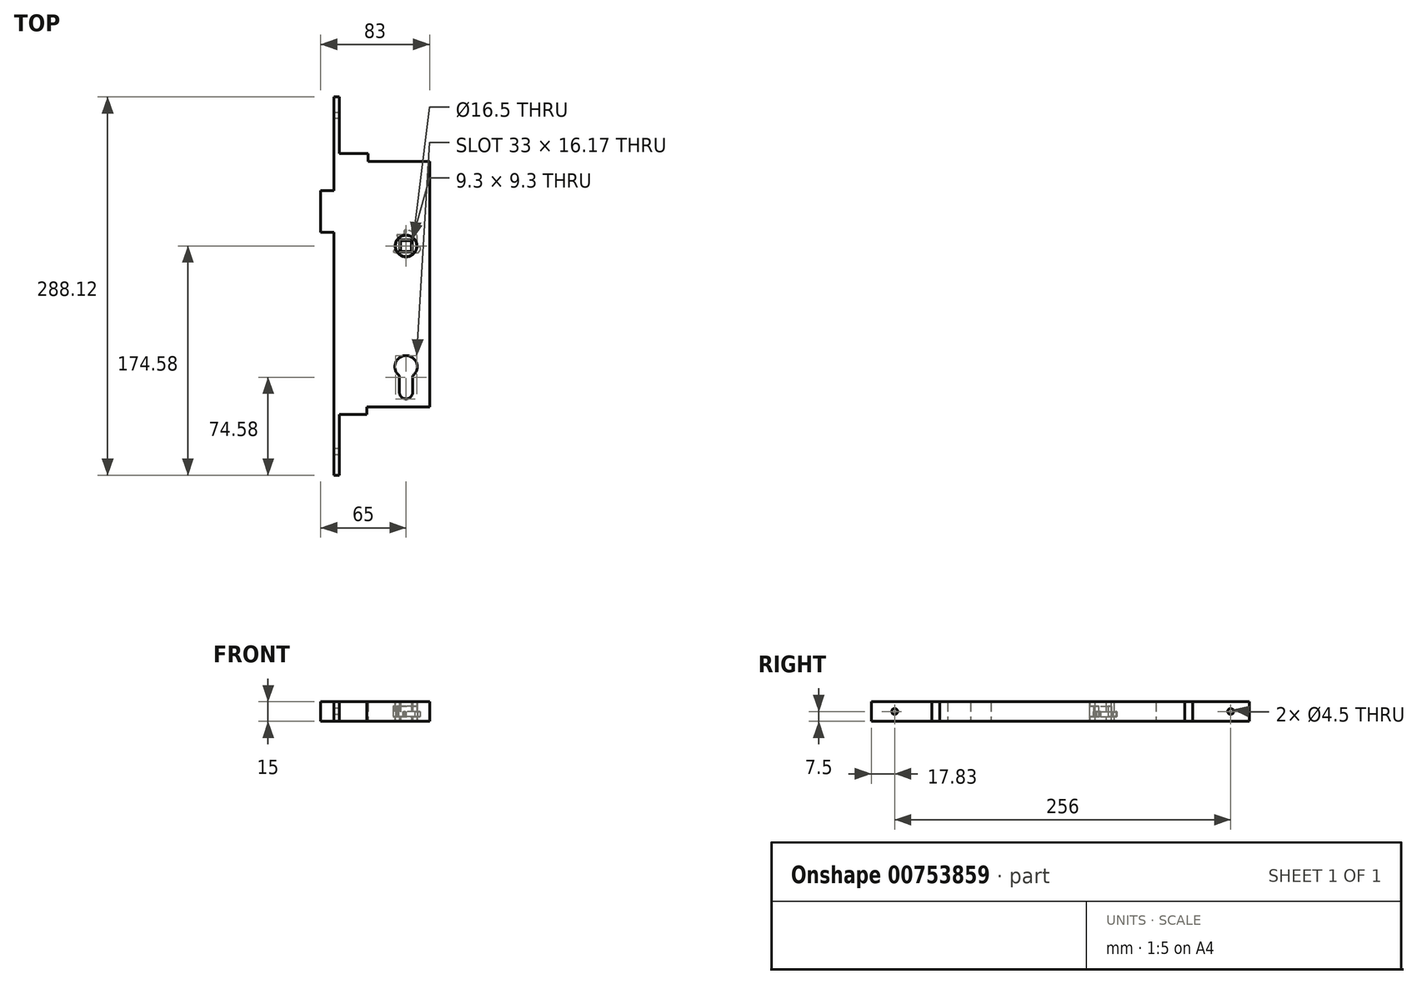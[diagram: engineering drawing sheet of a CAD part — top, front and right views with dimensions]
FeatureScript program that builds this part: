
annotation { "Feature Type Name" : "Feature", "Feature Type Description" : "" }
export const myFeature = defineFeature(function(context is Context, id is Id, definition is map)
    precondition{}
    {
        {
            var Q0;
            Q0=qCreatedBy(makeId("Top.planeOp"),FACE);
            var sketch = newSketch(context, id + "F0", { "sketchPlane" : qUnion([Q0])});
            skLineSegment(sketch, "E0.bottom", {"start": v(4.15, 4.15) * mm, "end": v(-4.15, 4.15) * mm});
            skLineSegment(sketch, "E0.top", {"start": v(4.15, -4.15) * mm, "end": v(-4.15, -4.15) * mm});
            skLineSegment(sketch, "E0.left", {"start": v(4.15, 4.15) * mm, "end": v(4.15, -4.15) * mm});
            skLineSegment(sketch, "E0.right", {"start": v(-4.15, 4.15) * mm, "end": v(-4.15, -4.15) * mm});
            skPoint(sketch, "E0.middle", {"position": v(0, 0) * mm});
            skCircle(sketch, "E1", {"center": v(0, 0) * mm, "radius": 8.15 * mm});
            skSolve(sketch);
        }
        {
            var Q0;
            Q0=makeQuery(id+"F0.imprint","IMPRINT",FACE,{"disambiguationData":[TD([[makeQuery(id+"F0.imprint","IMPRINT",EDGE,{"derivedFrom":sQuery(id+"F0.wireOp",EDGE,"E0.bottom")}),-1.0]])]});
            extrude(context, id + "F1", {"entities" : qUnion([Q0]), "depth" : 3.5 * mm, "offsetDistance" : 25 * mm});
        }
        {
            var Q0;
            Q0=makeQuery(id+"F1.opExtrude","CAP_FACE",FACE,{"disambiguationData":[OSD([sQuery(id+"F0.wireOp",EDGE,"E0.bottom"),sQuery(id+"F0.wireOp",EDGE,"E0.top"),sQuery(id+"F0.wireOp",EDGE,"E0.left"),sQuery(id+"F0.wireOp",EDGE,"E0.right"),sQuery(id+"F0.wireOp",EDGE,"E1")])],"isStart":false});
            var sketch = newSketch(context, id + "F2", { "sketchPlane" : qUnion([Q0])});
            skCircle(sketch, "E2", {"center": v(0, 0) * mm, "radius": 8.53 * mm});
            skLineSegment(sketch, "E3", {"start": v(-4.15, 4.15) * mm, "end": v(7.23, -7.2) * mm, "construction": true});
            skLineSegment(sketch, "E4", {"start": v(7.23, -7.2) * mm, "end": v(-8.21, 8.2) * mm, "construction": true});
            skLineSegment(sketch, "E5", {"start": v(0, 0) * mm, "end": v(7.32, 7.33) * mm, "construction": true});
            skLineSegment(sketch, "E6", {"start": v(7.32, 7.33) * mm, "end": v(-7.76, -7.78) * mm, "construction": true});
            skLineSegment(sketch, "E7", {"start": v(0, 8.53) * mm, "end": v(-7.56, 8.53) * mm});
            skLineSegment(sketch, "E8", {"start": v(8.53, 0) * mm, "end": v(8.53, 8) * mm});
            skLineSegment(sketch, "E9", {"start": v(-7.56, 8.53) * mm, "end": v(-5.76, 5.76) * mm});
            skPoint(sketch, "E10", {"position": v(-2.56, 8.53) * mm});
            skLineSegment(sketch, "E11", {"start": v(8.53, 0) * mm, "end": v(10.8, -1.06) * mm});
            skLineSegment(sketch, "E12", {"start": v(10.8, -1.06) * mm, "end": v(10.8, -3.06) * mm});
            skLineSegment(sketch, "E13", {"start": v(9.01, -5.5) * mm, "end": v(6.51, -5.5) * mm});
            skPoint(sketch, "E14", {"position": v(9.01, -5.5) * mm});
            skPoint(sketch, "E15", {"position": v(10.8, -3.06) * mm});
            skLineSegment(sketch, "E16", {"start": v(10.8, -3.06) * mm, "end": v(9.01, -5.5) * mm});
            skPoint(sketch, "E17", {"position": v(0, 12.53) * mm});
            skLineSegment(sketch, "E18", {"start": v(8.53, 0) * mm, "end": v(8.53, -5.5) * mm, "construction": true});
            skArc(sketch, "E19", {"start": v(8.53, 8) * mm, "mid": v(4.54, 10.78) * mm, "end": v(0, 12.53) * mm});
            skPoint(sketch, "E20", {"position": v(-1.56, 9.53) * mm});
            skLineSegment(sketch, "E21", {"start": v(-2.56, 8.53) * mm, "end": v(-1.56, 9.53) * mm});
            skPoint(sketch, "E22", {"position": v(-0.56, 9.53) * mm});
            skPoint(sketch, "E23", {"position": v(0, 11.53) * mm});
            skArc(sketch, "E24", {"start": v(-0.56, 9.53) * mm, "mid": v(-0.09, 10.47) * mm, "end": v(0, 11.53) * mm});
            skLineSegment(sketch, "E25", {"start": v(0, 12.53) * mm, "end": v(0, 11.53) * mm});
            skLineSegment(sketch, "E26", {"start": v(-0.56, 9.53) * mm, "end": v(-1.56, 9.53) * mm});
            skLineSegment(sketch, "E27", {"start": v(0, -4.4) * mm, "end": v(-13.74, -4.4) * mm, "construction": true});
            skPoint(sketch, "E28", {"position": v(-9.86, -4.4) * mm});
            skPoint(sketch, "E29", {"position": v(-6.86, -4.4) * mm});
            skLineSegment(sketch, "E30", {"start": v(-8.03, -1.4) * mm, "end": v(-8.03, -4.4) * mm, "construction": true});
            skLineSegment(sketch, "E31", {"start": v(-8.03, -1.4) * mm, "end": v(-9.86, -4.4) * mm});
            skLineSegment(sketch, "E32", {"start": v(-9.86, -4.4) * mm, "end": v(-8, -5.13) * mm});
            skLineSegment(sketch, "E33", {"start": v(-8, -5.13) * mm, "end": v(-6.74, -5.23) * mm});
            skSolve(sketch);
        }
        {
            var Q0;
            {var subQ0=sQuery(id+"F2.wireOp",EDGE,"E2");var subQ5=makeQuery(id+"F2.imprint","INTERSECT",VERTEX,{"derivedFrom":[subQ0,sQuery(id+"F2.wireOp",EDGE,"E7")]});Q0=makeQuery(id+"F2.imprint","IMPRINT",FACE,{"disambiguationData":[TD([[makeQuery(id+"F2.imprint","IMPRINT",EDGE,{"disambiguationData":[TD([[subQ5,-1.0]])],"derivedFrom":subQ0}),1.0]])]});}
            var Q1;
            {var subQ0=sQuery(id+"F2.wireOp",EDGE,"E7");var subQ1=sQuery(id+"F2.wireOp",EDGE,"E2");var subQ2=makeQuery(id+"F2.imprint","INTERSECT",VERTEX,{"derivedFrom":[subQ1,subQ0]});Q1=makeQuery(id+"F2.imprint","IMPRINT",FACE,{"disambiguationData":[TD([[makeQuery(id+"F2.imprint","IMPRINT",EDGE,{"disambiguationData":[TD([[subQ2,-1.0]])],"derivedFrom":subQ1}),-1.0]])]});}
            var Q2;
            {var subQ0=sQuery(id+"F2.wireOp",EDGE,"E8");Q2=makeQuery(id+"F2.imprint","IMPRINT",FACE,{"disambiguationData":[TD([[makeQuery(id+"F2.imprint","IMPRINT",EDGE,{"derivedFrom":subQ0}),1.0]])]});}
            var Q3;
            {var subQ1=sQuery(id+"F2.wireOp",EDGE,"E11");Q3=makeQuery(id+"F2.imprint","IMPRINT",FACE,{"disambiguationData":[TD([[makeQuery(id+"F2.imprint","IMPRINT",EDGE,{"derivedFrom":subQ1}),-1.0]])]});}
            var Q4;
            {var subQ4=sQuery(id+"F2.wireOp",EDGE,"E32");Q4=makeQuery(id+"F2.imprint","IMPRINT",FACE,{"disambiguationData":[TD([[makeQuery(id+"F2.imprint","IMPRINT",EDGE,{"derivedFrom":subQ4}),1.0]])]});}
            var Q5;
            Q5=makeQuery(id+"F2.imprint","IMPRINT",FACE,{"disambiguationData":[TD([[makeQuery(id+"F2.imprint","IMPRINT",EDGE,{"derivedFrom":makeQuery(id+"F1.opExtrude","CAP_EDGE",EDGE,{"disambiguationData":[OSD([sQuery(id+"F0.wireOp",EDGE,"E0.bottom")])],"isStart":false})}),-1.0]])]});
            extrude(context, id + "F3", {"entities" : qUnion([Q0, Q1, Q2, Q3, Q4, Q5]), "operationType" : NewBodyOperationType.ADD, "depth" : 3.8 * mm, "offsetDistance" : 25 * mm});
        }
        {
            var Q0;
            Q0=makeQuery(id+"F2.imprint","IMPRINT",FACE,{"disambiguationData":[TD([[makeQuery(id+"F2.imprint","IMPRINT",EDGE,{"derivedFrom":makeQuery(id+"F1.opExtrude","CAP_EDGE",EDGE,{"disambiguationData":[OSD([sQuery(id+"F0.wireOp",EDGE,"E0.bottom")])],"isStart":false})}),-1.0]])]});
            extrude(context, id + "F4", {"entities" : qUnion([Q0]), "operationType" : NewBodyOperationType.ADD, "depth" : 11.5 * mm, "offsetDistance" : 25 * mm});
        }
        {
            var Q0;
            {var subQ0=sQuery(id+"F2.wireOp",EDGE,"E2");var subQ5=makeQuery(id+"F2.imprint","INTERSECT",VERTEX,{"derivedFrom":[subQ0,sQuery(id+"F2.wireOp",EDGE,"E7")]});Q0=makeQuery(id+"F2.imprint","IMPRINT",FACE,{"disambiguationData":[TD([[makeQuery(id+"F2.imprint","IMPRINT",EDGE,{"disambiguationData":[TD([[subQ5,-1.0]])],"derivedFrom":subQ0}),1.0]])]});}
            var Q1;
            {var subQ0=sQuery(id+"F2.wireOp",EDGE,"E7");var subQ1=sQuery(id+"F2.wireOp",EDGE,"E2");var subQ2=makeQuery(id+"F2.imprint","INTERSECT",VERTEX,{"derivedFrom":[subQ1,subQ0]});Q1=makeQuery(id+"F2.imprint","IMPRINT",FACE,{"disambiguationData":[TD([[makeQuery(id+"F2.imprint","IMPRINT",EDGE,{"disambiguationData":[TD([[subQ2,-1.0]])],"derivedFrom":subQ1}),-1.0]])]});}
            var Q2;
            {var subQ4=sQuery(id+"F2.wireOp",EDGE,"E32");Q2=makeQuery(id+"F2.imprint","IMPRINT",FACE,{"disambiguationData":[TD([[makeQuery(id+"F2.imprint","IMPRINT",EDGE,{"derivedFrom":subQ4}),1.0]])]});}
            extrude(context, id + "F5", {"entities" : qUnion([Q0, Q1, Q2]), "operationType" : NewBodyOperationType.ADD, "depth" : 8 * mm, "offsetDistance" : 25 * mm});
        }
        {
            var Q0;
            {var subQ0=sQuery(id+"F2.wireOp",EDGE,"E9");var subQ1=sQuery(id+"F2.wireOp",EDGE,"E7");Q0=makeQuery(id+"F5.boolean.opBoolean","MERGE",EDGE,{"derivedFrom":[makeQuery(id+"F3.opExtrude","SWEPT_EDGE",EDGE,{"disambiguationData":[OSD([subQ1,subQ0])]}),makeQuery(id+"F5.opExtrude","SWEPT_EDGE",EDGE,{"disambiguationData":[OSD([subQ1,subQ0])]})]});}
            fillet(context, id + "F6", {"entities" : qUnion([Q0]), "radius" : 0.5 * mm, "tangentPropagation" : true, "allowEdgeOverflow" : false});
        }
        {
            var Q0;
            Q0=makeQuery(id+"F3.opExtrude","SWEPT_FACE",FACE,{"disambiguationData":[OSD([sQuery(id+"F2.wireOp",EDGE,"E11")])]});
            var sketch = newSketch(context, id + "F7", { "sketchPlane" : qUnion([Q0])});
            skLineSegment(sketch, "E34", {"start": v(-7.73, 3.5) * mm, "end": v(-10.23, 5.3) * mm});
            skLineSegment(sketch, "E35", {"start": v(-7.73, 3.5) * mm, "end": v(-12.23, 6.74) * mm});
            skLineSegment(sketch, "E36", {"start": v(-12.23, 6.74) * mm, "end": v(-12.03, 1.79) * mm});
            skLineSegment(sketch, "E37", {"start": v(-12.03, 1.79) * mm, "end": v(-7.73, 3.5) * mm});
            skSolve(sketch);
        }
        {
            var Q0;
            Q0=makeQuery(id+"F4.opExtrude","CAP_EDGE",EDGE,{"disambiguationData":[OSD([sQuery(id+"F0.wireOp",EDGE,"E0.left")])],"isStart":false});
            var Q1;
            Q1=makeQuery(id+"F4.opExtrude","CAP_EDGE",EDGE,{"disambiguationData":[OSD([sQuery(id+"F0.wireOp",EDGE,"E0.bottom")])],"isStart":false});
            var Q2;
            Q2=makeQuery(id+"F4.opExtrude","CAP_EDGE",EDGE,{"disambiguationData":[OSD([sQuery(id+"F0.wireOp",EDGE,"E0.right")])],"isStart":false});
            var Q3;
            Q3=makeQuery(id+"F4.opExtrude","CAP_EDGE",EDGE,{"disambiguationData":[OSD([sQuery(id+"F0.wireOp",EDGE,"E0.top")])],"isStart":false});
            var Q4;
            Q4=makeQuery(id+"F1.opExtrude","CAP_EDGE",EDGE,{"disambiguationData":[OSD([sQuery(id+"F0.wireOp",EDGE,"E0.left")])],"isStart":true});
            var Q5;
            Q5=makeQuery(id+"F1.opExtrude","CAP_EDGE",EDGE,{"disambiguationData":[OSD([sQuery(id+"F0.wireOp",EDGE,"E0.right")])],"isStart":true});
            var Q6;
            Q6=makeQuery(id+"F1.opExtrude","CAP_EDGE",EDGE,{"disambiguationData":[OSD([sQuery(id+"F0.wireOp",EDGE,"E0.bottom")])],"isStart":true});
            var Q7;
            Q7=makeQuery(id+"F1.opExtrude","CAP_EDGE",EDGE,{"disambiguationData":[OSD([sQuery(id+"F0.wireOp",EDGE,"E0.top")])],"isStart":true});
            chamfer(context, id + "F8", {"entities" : qUnion([Q0, Q1, Q2, Q3, Q4, Q5, Q6, Q7]), "width" : 0.5 * mm, "tangentPropagation" : true});
        }
        {
            var Q0;
            Q0=makeQuery(id+"F3.opExtrude","SWEPT_FACE",FACE,{"disambiguationData":[OSD([sQuery(id+"F2.wireOp",EDGE,"E25")])]});
            var sketch = newSketch(context, id + "F9", { "sketchPlane" : qUnion([Q0])});
            skArc(sketch, "E38", {"start": v(-12.29, 5.38) * mm, "mid": v(-10.54, 3.63) * mm, "end": v(-8.79, 5.38) * mm});
            skPoint(sketch, "E38.centerSnap0", {"position": v(-11.53, 5.38) * mm});
            skLineSegment(sketch, "E39", {"start": v(-8.79, 5.38) * mm, "end": v(-12.29, 5.38) * mm});
            skSolve(sketch);
        }
        {
            var Q0;
            {var subQ0=sQuery(id+"F9.wireOp",EDGE,"E39");var subQ1=sQuery(id+"F9.wireOp",EDGE,"E38");var subQ2=makeQuery(id+"F9.imprint","INTERSECT",VERTEX,{"disambiguationData":[OD(0.0)],"derivedFrom":[subQ1,subQ0]});Q0=makeQuery(id+"F9.imprint","IMPRINT",FACE,{"disambiguationData":[TD([[makeQuery(id+"F9.imprint","IMPRINT",EDGE,{"disambiguationData":[TD([[subQ2,-1.0]])],"derivedFrom":subQ1}),1.0]])]});}
            var Q1;
            {var subQ0=sQuery(id+"F9.wireOp",EDGE,"E39");var subQ1=sQuery(id+"F9.wireOp",EDGE,"E38");var subQ2=makeQuery(id+"F9.imprint","INTERSECT",VERTEX,{"disambiguationData":[OD(1.0)],"derivedFrom":[subQ1,subQ0]});Q1=makeQuery(id+"F9.imprint","IMPRINT",FACE,{"disambiguationData":[TD([[makeQuery(id+"F9.imprint","IMPRINT",EDGE,{"disambiguationData":[TD([[subQ2,1.0]])],"derivedFrom":subQ1}),1.0]])]});}
            var Q2;
            Q2=sQuery(id+"F9.wireOp",EDGE,"E39");
            revolve(context, id + "F10", {"operationType" : NewBodyOperationType.REMOVE, "surfaceOperationType" : NewSurfaceOperationType.NEW, "entities" : qUnion([Q0, Q1]), "axis" : qUnion([Q2]), "revolveType" : RevolveType.FULL, "oppositeDirection" : true});
        }
        {
            var Q0;
            Q0=qCreatedBy(makeId("Top.planeOp"),FACE);
            var sketch = newSketch(context, id + "F11", { "sketchPlane" : qUnion([Q0])});
            skLineSegment(sketch, "E40", {"start": v(0, 0) * mm, "end": v(0, -92) * mm, "construction": true});
            skArc(sketch, "E41", {"start": v(5, -98.87) * mm, "mid": v(0, -83.5) * mm, "end": v(-5, -98.87) * mm});
            skPoint(sketch, "E42", {"position": v(0, -83.5) * mm});
            skLineSegment(sketch, "E43", {"start": v(0, -83.5) * mm, "end": v(0, -116.5) * mm, "construction": true});
            skLineSegment(sketch, "E44", {"start": v(-5, -98.87) * mm, "end": v(-5, -111.5) * mm});
            skArc(sketch, "E45", {"start": v(-5, -111.5) * mm, "mid": v(0, -116.5) * mm, "end": v(5, -111.5) * mm});
            skLineSegment(sketch, "E46.MirrorCS", {"start": v(5, -98.87) * mm, "end": v(5, -111.5) * mm});
            skCircle(sketch, "E47", {"center": v(0, 0) * mm, "radius": 8.25 * mm});
            skLineSegment(sketch, "E48", {"start": v(0, 0) * mm, "end": v(-55, 0) * mm, "construction": true});
            skLineSegment(sketch, "E49", {"start": v(0, 0) * mm, "end": v(18, 0) * mm, "construction": true});
            skLineSegment(sketch, "E50", {"start": v(0, -116.5) * mm, "end": v(0, -122.5) * mm, "construction": true});
            skLineSegment(sketch, "E51", {"start": v(-55, 0) * mm, "end": v(-55, -122.5) * mm});
            skLineSegment(sketch, "E52", {"start": v(-30, -122.5) * mm, "end": v(18, -122.5) * mm});
            skLineSegment(sketch, "E53", {"start": v(18, -122.5) * mm, "end": v(18, 0) * mm});
            skPoint(sketch, "E54", {"position": v(-30, -122.5) * mm});
            skLineSegment(sketch, "E55", {"start": v(-30, -122.5) * mm, "end": v(-30, -128.5) * mm});
            skLineSegment(sketch, "E56", {"start": v(-30, -128.5) * mm, "end": v(-51, -128.5) * mm});
            skLineSegment(sketch, "E57", {"start": v(-55, -128.5) * mm, "end": v(-55, -122.5) * mm});
            skLineSegment(sketch, "E58", {"start": v(0, 0) * mm, "end": v(0, 64.25) * mm, "construction": true});
            skLineSegment(sketch, "E59", {"start": v(18, 0) * mm, "end": v(18, 64.25) * mm});
            skLineSegment(sketch, "E60", {"start": v(18, 64.25) * mm, "end": v(-29, 64.25) * mm});
            skLineSegment(sketch, "E61", {"start": v(-55, 64.25) * mm, "end": v(-55, 42.25) * mm});
            skPoint(sketch, "E62", {"position": v(-29, 64.25) * mm});
            skLineSegment(sketch, "E63", {"start": v(-29, 64.25) * mm, "end": v(-29, 70.25) * mm});
            skLineSegment(sketch, "E64", {"start": v(-29, 70.25) * mm, "end": v(-51, 70.25) * mm});
            skLineSegment(sketch, "E65", {"start": v(-55, 70.25) * mm, "end": v(-55, 64.25) * mm});
            skPoint(sketch, "E66", {"position": v(0, 8.25) * mm});
            skLineSegment(sketch, "E67", {"start": v(0, 8.25) * mm, "end": v(-68.27, 8.25) * mm, "construction": true});
            skPoint(sketch, "E68", {"position": v(-55, 10.25) * mm});
            skPoint(sketch, "E69", {"position": v(-55, 42.25) * mm});
            skLineSegment(sketch, "E70", {"start": v(-55, 42.25) * mm, "end": v(-65, 42.25) * mm});
            skLineSegment(sketch, "E71", {"start": v(-65, 42.25) * mm, "end": v(-65, 10.25) * mm});
            skLineSegment(sketch, "E72", {"start": v(-65, 10.25) * mm, "end": v(-55, 10.25) * mm});
            skLineSegment(sketch, "E73.trimOffspring", {"start": v(-55, 10.25) * mm, "end": v(-55, 0) * mm});
            skPoint(sketch, "E74", {"position": v(-55, 99.25) * mm});
            skLineSegment(sketch, "E75", {"start": v(-55, 70.25) * mm, "end": v(-55, 113.54) * mm});
            skLineSegment(sketch, "E76", {"start": v(-55, 113.54) * mm, "end": v(-51, 113.54) * mm});
            skLineSegment(sketch, "E77", {"start": v(-51, 113.54) * mm, "end": v(-51, 70.25) * mm});
            skLineSegment(sketch, "E78", {"start": v(-55, 99.25) * mm, "end": v(-51, 99.25) * mm, "construction": true});
            skLineSegment(sketch, "E79", {"start": v(-45.3, 99.25) * mm, "end": v(-65.3, 99.25) * mm, "construction": true});
            skPoint(sketch, "E80", {"position": v(-55, -156.75) * mm});
            skLineSegment(sketch, "E81", {"start": v(-55, -128.5) * mm, "end": v(-55, -174.58) * mm});
            skLineSegment(sketch, "E82", {"start": v(-55, -174.58) * mm, "end": v(-51, -174.58) * mm});
            skLineSegment(sketch, "E83", {"start": v(-51, -174.58) * mm, "end": v(-51, -128.5) * mm});
            skLineSegment(sketch, "E84", {"start": v(-62.14, -156.75) * mm, "end": v(-42.14, -156.75) * mm, "construction": true});
            skSolve(sketch);
        }
        {
            var Q0;
            Q0=makeQuery(id+"F11.imprint","IMPRINT",FACE,{"disambiguationData":[TD([[makeQuery(id+"F11.imprint","IMPRINT",EDGE,{"derivedFrom":sQuery(id+"F11.wireOp",EDGE,"E41")}),-1.0]])]});
            var Q1;
            Q1=makeQuery(id+"F4.opExtrude","CAP_FACE",FACE,{"disambiguationData":[OSD([sQuery(id+"F0.wireOp",EDGE,"E0.bottom"),sQuery(id+"F0.wireOp",EDGE,"E0.top"),sQuery(id+"F0.wireOp",EDGE,"E0.left"),sQuery(id+"F0.wireOp",EDGE,"E0.right"),sQuery(id+"F0.wireOp",EDGE,"E1")])],"isStart":false});
            extrude(context, id + "F12", {"entities" : qUnion([Q0]), "endBound" : BoundingType.UP_TO_SURFACE, "depth" : 25 * mm, "endBoundEntityFace" : qUnion([Q1]), "offsetDistance" : 25 * mm});
        }
        {
            var Q0;
            Q0=makeQuery(id+"F12.opExtrude","SWEPT_FACE",FACE,{"disambiguationData":[OSD([sQuery(id+"F11.wireOp",EDGE,"E61"),sQuery(id+"F11.wireOp",EDGE,"E65"),sQuery(id+"F11.wireOp",EDGE,"E75")])]});
            var sketch = newSketch(context, id + "F13", { "sketchPlane" : qUnion([Q0])});
            skLineSegment(sketch, "E85", {"start": v(-99.25, -7.06) * mm, "end": v(-99.25, 22.06) * mm, "construction": true});
            skPoint(sketch, "E86", {"position": v(-99.25, 7.5) * mm});
            skCircle(sketch, "E87", {"center": v(-99.25, 7.5) * mm, "radius": 2.25 * mm});
            skLineSegment(sketch, "E88", {"start": v(156.75, -5.16) * mm, "end": v(156.75, 20.16) * mm, "construction": true});
            skPoint(sketch, "E89", {"position": v(156.75, 7.5) * mm});
            skCircle(sketch, "E90", {"center": v(156.75, 7.5) * mm, "radius": 2.25 * mm});
            skSolve(sketch);
        }
        {
            var Q0;
            Q0=makeQuery(id+"F13.imprint","IMPRINT",FACE,{"disambiguationData":[TD([[makeQuery(id+"F13.imprint","IMPRINT",EDGE,{"derivedFrom":sQuery(id+"F13.wireOp",EDGE,"E90")}),1.0]])]});
            var Q1;
            Q1=makeQuery(id+"F13.imprint","IMPRINT",FACE,{"disambiguationData":[TD([[makeQuery(id+"F13.imprint","IMPRINT",EDGE,{"derivedFrom":sQuery(id+"F13.wireOp",EDGE,"E87")}),1.0]])]});
            var Q2;
            Q2=makeQuery(id+"F12.opExtrude","SWEPT_FACE",FACE,{"disambiguationData":[OSD([sQuery(id+"F11.wireOp",EDGE,"E77")])]});
            extrude(context, id + "F14", {"entities" : qUnion([Q0, Q1]), "operationType" : NewBodyOperationType.REMOVE, "endBound" : BoundingType.UP_TO_SURFACE, "oppositeDirection" : true, "depth" : 25 * mm, "endBoundEntityFace" : qUnion([Q2]), "offsetDistance" : 25 * mm});
        }
    });
